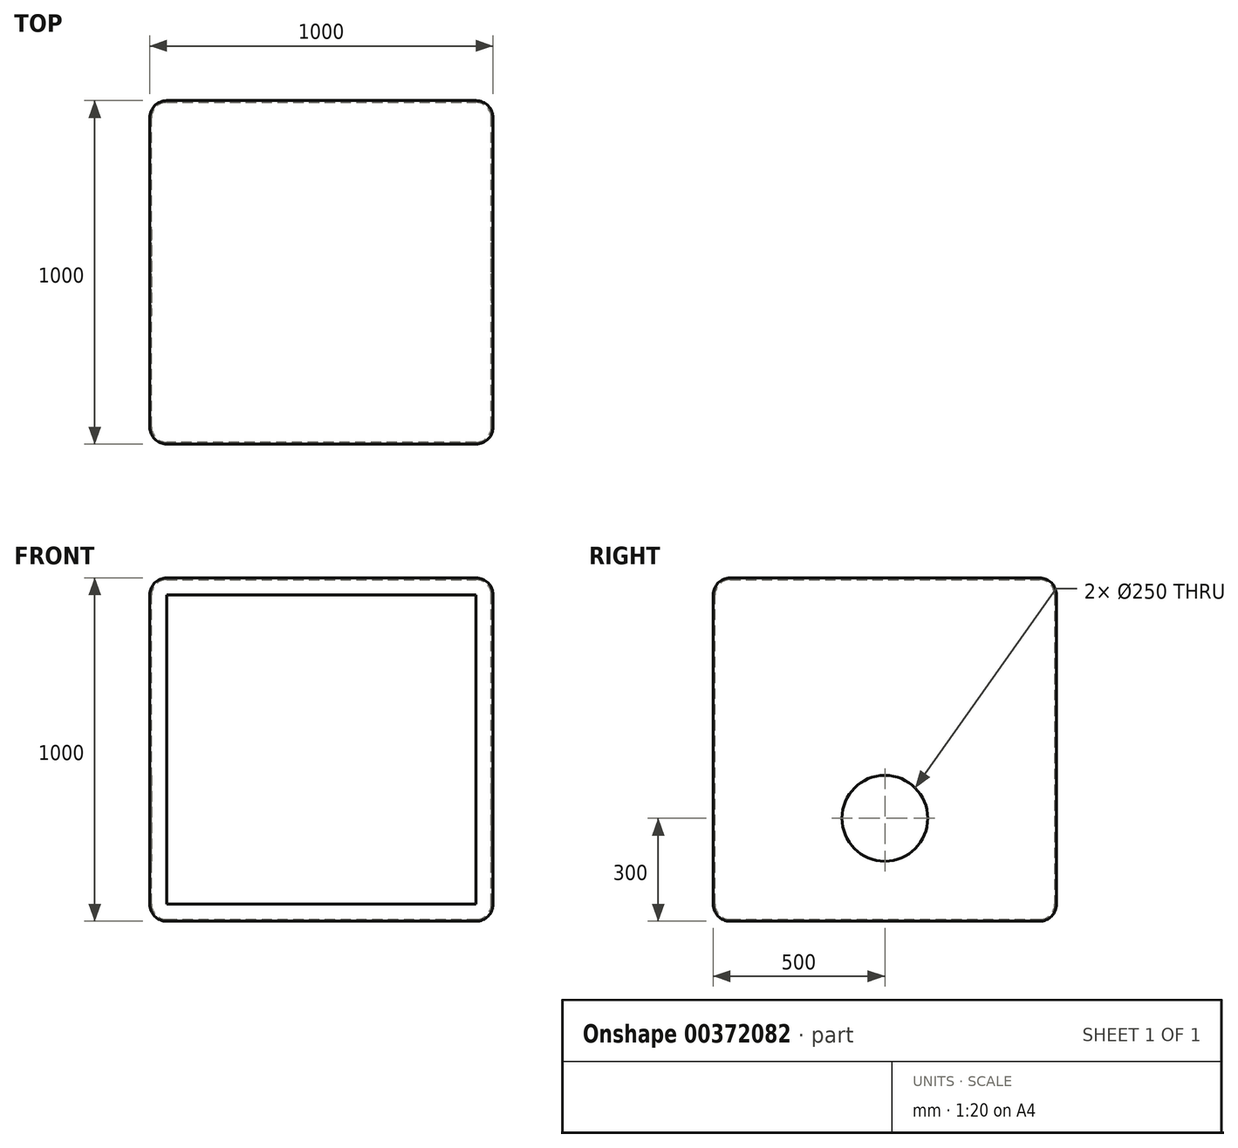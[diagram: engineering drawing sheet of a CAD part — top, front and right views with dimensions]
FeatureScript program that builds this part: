
annotation { "Feature Type Name" : "Feature", "Feature Type Description" : "" }
export const myFeature = defineFeature(function(context is Context, id is Id, definition is map)
    precondition{}
    {
        {
            var Q0;
            Q0=qCreatedBy(makeId("Top.planeOp"),FACE);
            var sketch = newSketch(context, id + "F0", { "sketchPlane" : qUnion([Q0])});
            skLineSegment(sketch, "E0.bottom", {"start": v(500, -500) * mm, "end": v(-500, -500) * mm});
            skLineSegment(sketch, "E0.top", {"start": v(500, 500) * mm, "end": v(-500, 500) * mm});
            skLineSegment(sketch, "E0.left", {"start": v(500, -500) * mm, "end": v(500, 500) * mm});
            skLineSegment(sketch, "E0.right", {"start": v(-500, -500) * mm, "end": v(-500, 500) * mm});
            skPoint(sketch, "E0.middle", {"position": v(0, 0) * mm});
            skSolve(sketch);
        }
        {
            var Q0;
            Q0 = qSketchRegion(id + "F0", true);
            extrude(context, id + "F1", {"entities" : qUnion([Q0]), "depth" : 1000 * mm});
        }
        {
            var Q0;
            Q0=makeQuery(id+"F1.opExtrude","CAP_EDGE",EDGE,{"disambiguationData":[OSD([sQuery(id+"F0.wireOp",EDGE,"E0.top")])],"isStart":false});
            var Q1;
            Q1=makeQuery(id+"F1.opExtrude","SWEPT_EDGE",EDGE,{"disambiguationData":[OSD([sQuery(id+"F0.wireOp",EDGE,"E0.top"),sQuery(id+"F0.wireOp",EDGE,"E0.right")])]});
            var Q2;
            Q2=makeQuery(id+"F1.opExtrude","CAP_EDGE",EDGE,{"disambiguationData":[OSD([sQuery(id+"F0.wireOp",EDGE,"E0.right")])],"isStart":false});
            var Q3;
            Q3=makeQuery(id+"F1.opExtrude","CAP_EDGE",EDGE,{"disambiguationData":[OSD([sQuery(id+"F0.wireOp",EDGE,"E0.left")])],"isStart":false});
            var Q4;
            Q4=makeQuery(id+"F1.opExtrude","SWEPT_EDGE",EDGE,{"disambiguationData":[OSD([sQuery(id+"F0.wireOp",EDGE,"E0.top"),sQuery(id+"F0.wireOp",EDGE,"E0.left")])]});
            var Q5;
            Q5=makeQuery(id+"F1.opExtrude","CAP_EDGE",EDGE,{"disambiguationData":[OSD([sQuery(id+"F0.wireOp",EDGE,"E0.bottom")])],"isStart":false});
            var Q6;
            Q6=makeQuery(id+"F1.opExtrude","SWEPT_EDGE",EDGE,{"disambiguationData":[OSD([sQuery(id+"F0.wireOp",EDGE,"E0.bottom"),sQuery(id+"F0.wireOp",EDGE,"E0.right")])]});
            var Q7;
            Q7=makeQuery(id+"F1.opExtrude","SWEPT_FACE",FACE,{"disambiguationData":[OSD([sQuery(id+"F0.wireOp",EDGE,"E0.left")])]});
            var Q8;
            Q8=makeQuery(id+"F1.opExtrude","CAP_FACE",FACE,{"disambiguationData":[OSD([sQuery(id+"F0.wireOp",EDGE,"E0.bottom"),sQuery(id+"F0.wireOp",EDGE,"E0.top"),sQuery(id+"F0.wireOp",EDGE,"E0.left"),sQuery(id+"F0.wireOp",EDGE,"E0.right")])],"isStart":true});
            fillet(context, id + "F2", {"entities" : qUnion([Q0, Q1, Q2, Q3, Q4, Q5, Q6, Q7, Q8]), "radius" : 50 * mm, "tangentPropagation" : true, "allowEdgeOverflow" : false});
        }
        {
            var Q0;
            Q0=makeQuery(id+"F1.opExtrude","SWEPT_FACE",FACE,{"disambiguationData":[OSD([sQuery(id+"F0.wireOp",EDGE,"E0.bottom")])]});
            shell(context, id + "F3", {"entities" : qUnion([Q0]), "thickness" : 5 * mm});
        }
        {
            var Q0;
            Q0=qCreatedBy(makeId("Right.planeOp"),FACE);
            var sketch = newSketch(context, id + "F4", { "sketchPlane" : qUnion([Q0])});
            skCircle(sketch, "E1", {"center": v(0, 300) * mm, "radius": 125 * mm});
            skSolve(sketch);
        }
        {
            var Q0;
            Q0 = qSketchRegion(id + "F4", true);
            extrude(context, id + "F5", {"entities" : qUnion([Q0]), "operationType" : NewBodyOperationType.REMOVE, "endBound" : BoundingType.SYMMETRIC, "oppositeDirection" : true, "depth" : 1300 * mm});
        }
    });
